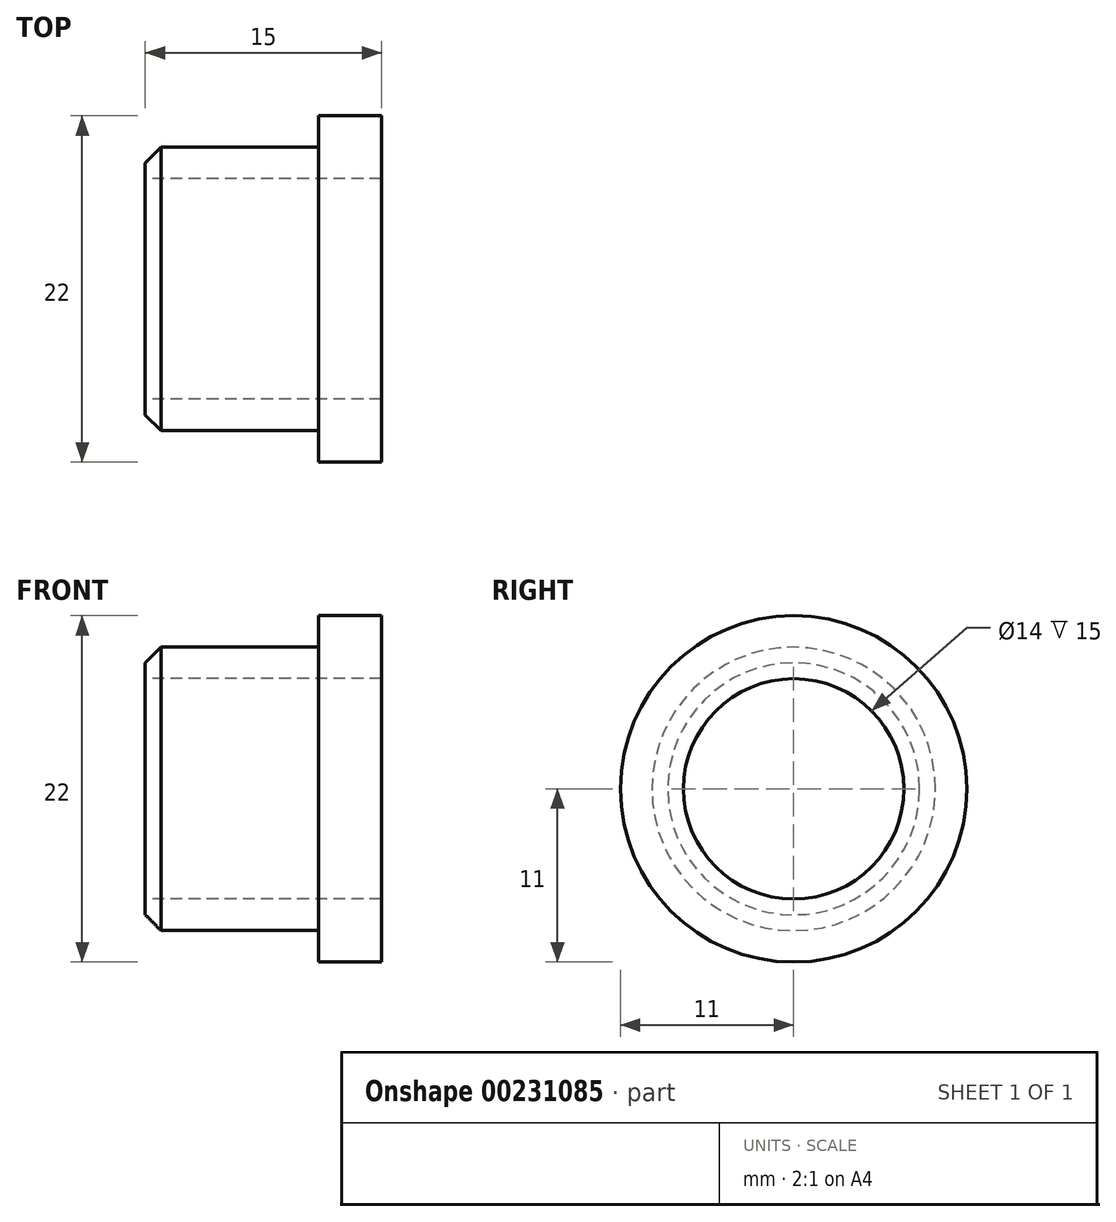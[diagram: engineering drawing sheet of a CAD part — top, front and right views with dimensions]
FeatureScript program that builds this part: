
annotation { "Feature Type Name" : "Feature", "Feature Type Description" : "" }
export const myFeature = defineFeature(function(context is Context, id is Id, definition is map)
    precondition{}
    {
        {
            var Q0;
            Q0=qCreatedBy(makeId("Front.planeOp"),FACE);
            var sketch = newSketch(context, id + "F0", { "sketchPlane" : qUnion([Q0])});
            skLineSegment(sketch, "E0", {"start": v(0, 0) * mm, "end": v(0, 9) * mm});
            skLineSegment(sketch, "E1", {"start": v(0, 9) * mm, "end": v(11, 9) * mm});
            skLineSegment(sketch, "E2", {"start": v(11, 9) * mm, "end": v(11, 11) * mm});
            skLineSegment(sketch, "E3", {"start": v(11, 11) * mm, "end": v(15, 11) * mm});
            skLineSegment(sketch, "E4", {"start": v(15, 11) * mm, "end": v(15, 0) * mm});
            skLineSegment(sketch, "E5", {"start": v(15, 0) * mm, "end": v(0, 0) * mm});
            skSolve(sketch);
        }
        {
            var Q0;
            Q0 = qSketchRegion(id + "F0", true);
            var Q1;
            Q1=sQuery(id+"F0.wireOp",EDGE,"E5");
            revolve(context, id + "F1", {"entities" : qUnion([Q0]), "axis" : qUnion([Q1]), "revolveType" : RevolveType.FULL});
        }
        {
            var Q0;
            Q0=qCreatedBy(makeId("Right.planeOp"),FACE);
            var sketch = newSketch(context, id + "F2", { "sketchPlane" : qUnion([Q0])});
            skCircle(sketch, "E6", {"center": v(0, 0) * mm, "radius": 7 * mm});
            skSolve(sketch);
        }
        {
            var Q0;
            Q0 = qSketchRegion(id + "F2", true);
            extrude(context, id + "F3", {"entities" : qUnion([Q0]), "operationType" : NewBodyOperationType.REMOVE, "depth" : 15 * mm});
        }
        {
            var Q0;
            Q0=makeQuery(id+"F1.opRevolve","SWEPT_EDGE",EDGE,{"disambiguationData":[OSD([sQuery(id+"F0.wireOp",EDGE,"E0"),sQuery(id+"F0.wireOp",EDGE,"E1")])]});
            chamfer(context, id + "F4", {"entities" : qUnion([Q0]), "width" : 1 * mm, "tangentPropagation" : true});
        }
    });
